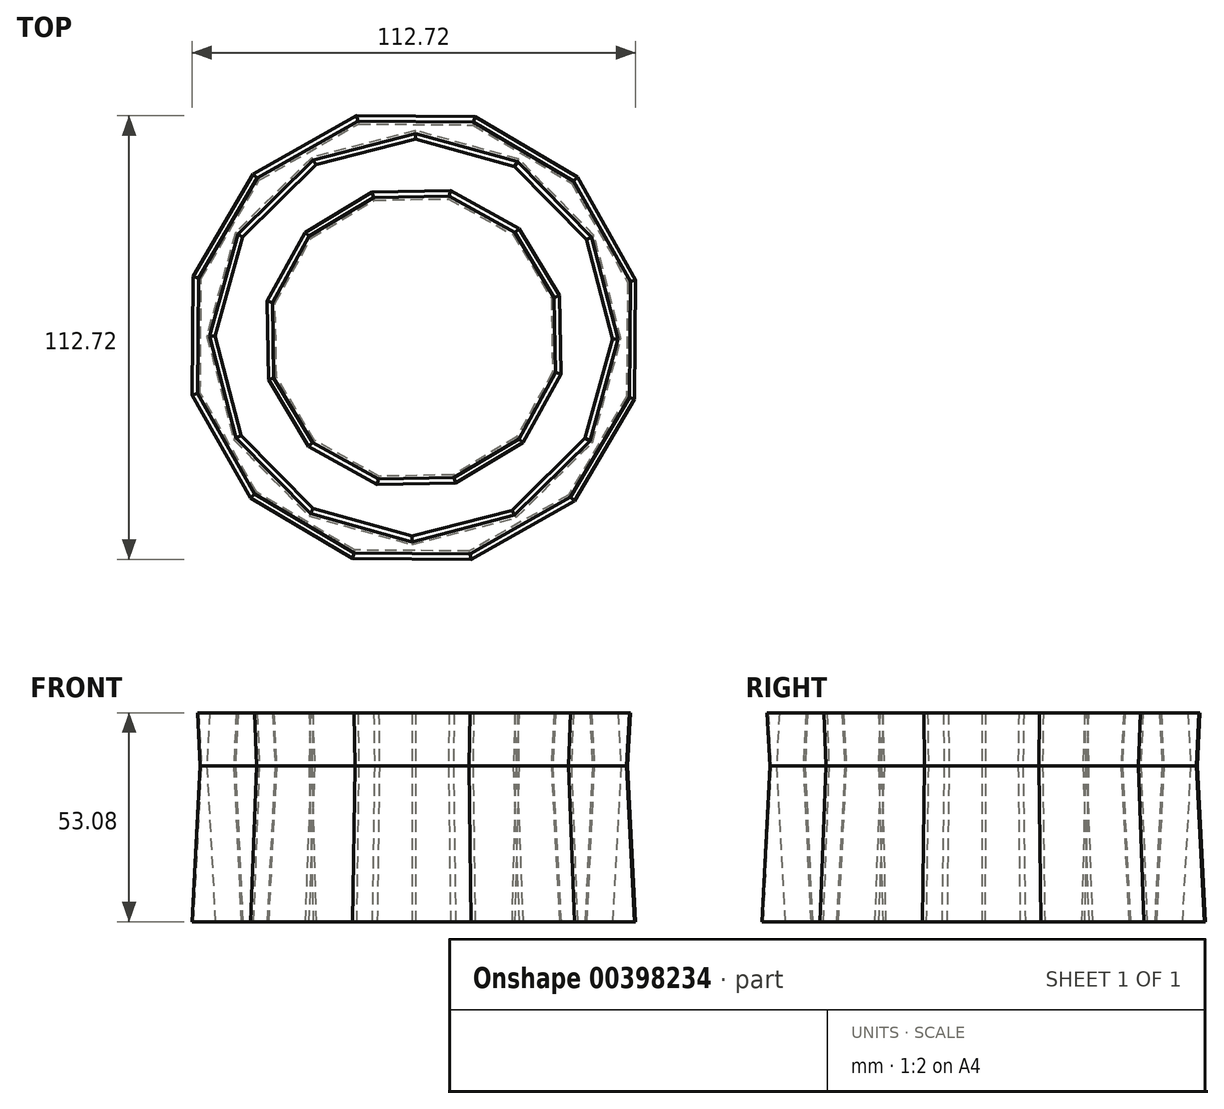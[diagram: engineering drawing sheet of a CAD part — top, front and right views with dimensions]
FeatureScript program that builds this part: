
annotation { "Feature Type Name" : "Feature", "Feature Type Description" : "" }
export const myFeature = defineFeature(function(context is Context, id is Id, definition is map)
    precondition{}
    {
        {
            var Q0;
            Q0=qCreatedBy(makeId("Top.planeOp"),FACE);
            var sketch = newSketch(context, id + "F0", { "sketchPlane" : qUnion([Q0])});
            skCircle(sketch, "E0.cCircle", {"center": v(0, 0) * mm, "radius": 54.15 * mm, "construction": true});
            skLineSegment(sketch, "E0.0", {"start": v(39.99, 39.3) * mm, "end": v(54.27, 14.03) * mm});
            skLineSegment(sketch, "E0.1", {"start": v(54.27, 14.03) * mm, "end": v(54.02, -14.98) * mm});
            skLineSegment(sketch, "E0.2", {"start": v(54.02, -14.98) * mm, "end": v(39.3, -39.99) * mm});
            skLineSegment(sketch, "E0.3", {"start": v(39.3, -39.99) * mm, "end": v(14.03, -54.27) * mm});
            skLineSegment(sketch, "E0.4", {"start": v(14.03, -54.27) * mm, "end": v(-14.98, -54.02) * mm});
            skLineSegment(sketch, "E0.5", {"start": v(-14.98, -54.02) * mm, "end": v(-39.99, -39.3) * mm});
            skLineSegment(sketch, "E0.6", {"start": v(-39.99, -39.3) * mm, "end": v(-54.27, -14.03) * mm});
            skLineSegment(sketch, "E0.7", {"start": v(-54.27, -14.03) * mm, "end": v(-54.02, 14.98) * mm});
            skLineSegment(sketch, "E0.8", {"start": v(-54.02, 14.98) * mm, "end": v(-39.3, 39.99) * mm});
            skLineSegment(sketch, "E0.9", {"start": v(-39.3, 39.99) * mm, "end": v(-14.03, 54.27) * mm});
            skLineSegment(sketch, "E0.10", {"start": v(-14.03, 54.27) * mm, "end": v(14.98, 54.02) * mm});
            skLineSegment(sketch, "E0.11", {"start": v(14.98, 54.02) * mm, "end": v(39.99, 39.3) * mm});
            skPoint(sketch, "E0.0.midPoint", {"position": v(47.13, 26.66) * mm});
            skCircle(sketch, "E1.cCircle", {"center": v(0, 0) * mm, "radius": 50.82 * mm, "construction": true});
            skLineSegment(sketch, "E1.0", {"start": v(45.77, 25.93) * mm, "end": v(52.6, -0.43) * mm});
            skLineSegment(sketch, "E1.1", {"start": v(52.6, -0.43) * mm, "end": v(45.35, -26.68) * mm});
            skLineSegment(sketch, "E1.2", {"start": v(45.35, -26.68) * mm, "end": v(25.93, -45.77) * mm});
            skLineSegment(sketch, "E1.3", {"start": v(25.93, -45.77) * mm, "end": v(-0.43, -52.6) * mm});
            skLineSegment(sketch, "E1.4", {"start": v(-0.43, -52.6) * mm, "end": v(-26.68, -45.35) * mm});
            skLineSegment(sketch, "E1.5", {"start": v(-26.68, -45.35) * mm, "end": v(-45.77, -25.93) * mm});
            skLineSegment(sketch, "E1.6", {"start": v(-45.77, -25.93) * mm, "end": v(-52.6, 0.43) * mm});
            skLineSegment(sketch, "E1.7", {"start": v(-52.6, 0.43) * mm, "end": v(-45.35, 26.68) * mm});
            skLineSegment(sketch, "E1.8", {"start": v(-45.35, 26.68) * mm, "end": v(-25.93, 45.77) * mm});
            skLineSegment(sketch, "E1.9", {"start": v(-25.93, 45.77) * mm, "end": v(0.43, 52.6) * mm});
            skLineSegment(sketch, "E1.10", {"start": v(0.43, 52.6) * mm, "end": v(26.68, 45.35) * mm});
            skLineSegment(sketch, "E1.11", {"start": v(26.68, 45.35) * mm, "end": v(45.77, 25.93) * mm});
            skPoint(sketch, "E1.0.midPoint", {"position": v(49.2, 12.75) * mm});
            skCircle(sketch, "E2.cCircle", {"center": v(0, 0) * mm, "radius": 44.72 * mm, "construction": true});
            skLineSegment(sketch, "E2.0", {"start": v(44.82, 11.6) * mm, "end": v(44.61, -12.37) * mm});
            skLineSegment(sketch, "E2.1", {"start": v(44.61, -12.37) * mm, "end": v(32.45, -33.02) * mm});
            skLineSegment(sketch, "E2.2", {"start": v(32.45, -33.02) * mm, "end": v(11.6, -44.82) * mm});
            skLineSegment(sketch, "E2.3", {"start": v(11.6, -44.82) * mm, "end": v(-12.37, -44.61) * mm});
            skLineSegment(sketch, "E2.4", {"start": v(-12.37, -44.61) * mm, "end": v(-33.02, -32.45) * mm});
            skLineSegment(sketch, "E2.5", {"start": v(-33.02, -32.45) * mm, "end": v(-44.82, -11.6) * mm});
            skLineSegment(sketch, "E2.6", {"start": v(-44.82, -11.6) * mm, "end": v(-44.61, 12.37) * mm});
            skLineSegment(sketch, "E2.7", {"start": v(-44.61, 12.37) * mm, "end": v(-32.45, 33.02) * mm});
            skLineSegment(sketch, "E2.8", {"start": v(-32.45, 33.02) * mm, "end": v(-11.6, 44.82) * mm});
            skLineSegment(sketch, "E2.9", {"start": v(-11.6, 44.82) * mm, "end": v(12.37, 44.61) * mm});
            skLineSegment(sketch, "E2.10", {"start": v(12.37, 44.61) * mm, "end": v(33.02, 32.45) * mm});
            skLineSegment(sketch, "E2.11", {"start": v(33.02, 32.45) * mm, "end": v(44.82, 11.6) * mm});
            skPoint(sketch, "E2.0.midPoint", {"position": v(44.71, -0.4) * mm});
            skCircle(sketch, "E3.cCircle", {"center": v(0, 0) * mm, "radius": 40.47 * mm, "construction": true});
            skLineSegment(sketch, "E3.0", {"start": v(36.41, 20.72) * mm, "end": v(41.9, -0.26) * mm});
            skLineSegment(sketch, "E3.1", {"start": v(41.9, -0.26) * mm, "end": v(36.15, -21.17) * mm});
            skLineSegment(sketch, "E3.2", {"start": v(36.15, -21.17) * mm, "end": v(20.72, -36.41) * mm});
            skLineSegment(sketch, "E3.3", {"start": v(20.72, -36.41) * mm, "end": v(-0.26, -41.9) * mm});
            skLineSegment(sketch, "E3.4", {"start": v(-0.26, -41.9) * mm, "end": v(-21.17, -36.15) * mm});
            skLineSegment(sketch, "E3.5", {"start": v(-21.17, -36.15) * mm, "end": v(-36.41, -20.72) * mm});
            skLineSegment(sketch, "E3.6", {"start": v(-36.41, -20.72) * mm, "end": v(-41.9, 0.26) * mm});
            skLineSegment(sketch, "E3.7", {"start": v(-41.9, 0.26) * mm, "end": v(-36.15, 21.17) * mm});
            skLineSegment(sketch, "E3.8", {"start": v(-36.15, 21.17) * mm, "end": v(-20.72, 36.41) * mm});
            skLineSegment(sketch, "E3.9", {"start": v(-20.72, 36.41) * mm, "end": v(0.26, 41.9) * mm});
            skLineSegment(sketch, "E3.10", {"start": v(0.26, 41.9) * mm, "end": v(21.17, 36.15) * mm});
            skLineSegment(sketch, "E3.11", {"start": v(21.17, 36.15) * mm, "end": v(36.41, 20.72) * mm});
            skPoint(sketch, "E3.0.midPoint", {"position": v(39.15, 10.23) * mm});
            skCircle(sketch, "E4.cCircle", {"center": v(0, 0) * mm, "radius": 35.08 * mm, "construction": true});
            skLineSegment(sketch, "E4.0", {"start": v(-35.24, 8.77) * mm, "end": v(-26.13, 25.22) * mm});
            skLineSegment(sketch, "E4.1", {"start": v(-26.13, 25.22) * mm, "end": v(-10.02, 34.9) * mm});
            skLineSegment(sketch, "E4.2", {"start": v(-10.02, 34.9) * mm, "end": v(8.77, 35.24) * mm});
            skLineSegment(sketch, "E4.3", {"start": v(8.77, 35.24) * mm, "end": v(25.22, 26.13) * mm});
            skLineSegment(sketch, "E4.4", {"start": v(25.22, 26.13) * mm, "end": v(34.9, 10.02) * mm});
            skLineSegment(sketch, "E4.5", {"start": v(34.9, 10.02) * mm, "end": v(35.24, -8.77) * mm});
            skLineSegment(sketch, "E4.6", {"start": v(35.24, -8.77) * mm, "end": v(26.13, -25.22) * mm});
            skLineSegment(sketch, "E4.7", {"start": v(26.13, -25.22) * mm, "end": v(10.02, -34.9) * mm});
            skLineSegment(sketch, "E4.8", {"start": v(10.02, -34.9) * mm, "end": v(-8.77, -35.24) * mm});
            skLineSegment(sketch, "E4.9", {"start": v(-8.77, -35.24) * mm, "end": v(-25.22, -26.13) * mm});
            skLineSegment(sketch, "E4.10", {"start": v(-25.22, -26.13) * mm, "end": v(-34.9, -10.02) * mm});
            skLineSegment(sketch, "E4.11", {"start": v(-34.9, -10.02) * mm, "end": v(-35.24, 8.77) * mm});
            skPoint(sketch, "E4.0.midPoint", {"position": v(-30.69, 17) * mm});
            skCircle(sketch, "E5.cCircle", {"center": v(0, 0) * mm, "radius": 29.08 * mm, "construction": true});
            skLineSegment(sketch, "E5.0", {"start": v(-16.79, 29.08) * mm, "end": v(16.79, 29.08) * mm});
            skLineSegment(sketch, "E5.1", {"start": v(16.79, 29.08) * mm, "end": v(33.58, 0) * mm});
            skLineSegment(sketch, "E5.2", {"start": v(33.58, 0) * mm, "end": v(16.79, -29.08) * mm});
            skLineSegment(sketch, "E5.3", {"start": v(16.79, -29.08) * mm, "end": v(-16.79, -29.08) * mm});
            skLineSegment(sketch, "E5.4", {"start": v(-16.79, -29.08) * mm, "end": v(-33.58, 0) * mm});
            skLineSegment(sketch, "E5.5", {"start": v(-33.58, 0) * mm, "end": v(-16.79, 29.08) * mm});
            skPoint(sketch, "E5.0.midPoint", {"position": v(0, 29.08) * mm});
            skCircle(sketch, "E6.cCircle", {"center": v(0, 0) * mm, "radius": 23.57 * mm, "construction": true});
            skLineSegment(sketch, "E6.0", {"start": v(-23.6, 13.55) * mm, "end": v(-0.07, 27.21) * mm});
            skLineSegment(sketch, "E6.1", {"start": v(-0.07, 27.21) * mm, "end": v(23.53, 13.67) * mm});
            skLineSegment(sketch, "E6.2", {"start": v(23.53, 13.67) * mm, "end": v(23.6, -13.55) * mm});
            skLineSegment(sketch, "E6.3", {"start": v(23.6, -13.55) * mm, "end": v(0.07, -27.21) * mm});
            skLineSegment(sketch, "E6.4", {"start": v(0.07, -27.21) * mm, "end": v(-23.53, -13.67) * mm});
            skLineSegment(sketch, "E6.5", {"start": v(-23.53, -13.67) * mm, "end": v(-23.6, 13.55) * mm});
            skPoint(sketch, "E6.0.midPoint", {"position": v(-11.84, 20.38) * mm});
            skCircle(sketch, "E7.cCircle", {"center": v(0, 0) * mm, "radius": 18.85 * mm, "construction": true});
            skLineSegment(sketch, "E7.0", {"start": v(11.61, 18.41) * mm, "end": v(21.75, -0.85) * mm});
            skLineSegment(sketch, "E7.1", {"start": v(21.75, -0.85) * mm, "end": v(10.14, -19.26) * mm});
            skLineSegment(sketch, "E7.2", {"start": v(10.14, -19.26) * mm, "end": v(-11.61, -18.41) * mm});
            skLineSegment(sketch, "E7.3", {"start": v(-11.61, -18.41) * mm, "end": v(-21.75, 0.85) * mm});
            skLineSegment(sketch, "E7.4", {"start": v(-21.75, 0.85) * mm, "end": v(-10.14, 19.26) * mm});
            skLineSegment(sketch, "E7.5", {"start": v(-10.14, 19.26) * mm, "end": v(11.61, 18.41) * mm});
            skPoint(sketch, "E7.0.midPoint", {"position": v(16.68, 8.78) * mm});
            skCircle(sketch, "E8.cCircle", {"center": v(0, 0) * mm, "radius": 14.7 * mm, "construction": true});
            skLineSegment(sketch, "E8.0", {"start": v(-8.28, 12.18) * mm, "end": v(-6.7, 13.12) * mm, "construction": true});
            skLineSegment(sketch, "E8.1", {"start": v(-6.7, 13.12) * mm, "end": v(-5, 13.85) * mm, "construction": true});
            skLineSegment(sketch, "E8.2", {"start": v(-5, 13.85) * mm, "end": v(-3.22, 14.37) * mm, "construction": true});
            skLineSegment(sketch, "E8.3", {"start": v(-3.22, 14.37) * mm, "end": v(-1.4, 14.66) * mm, "construction": true});
            skLineSegment(sketch, "E8.4", {"start": v(-1.4, 14.66) * mm, "end": v(0.46, 14.72) * mm, "construction": true});
            skLineSegment(sketch, "E8.5", {"start": v(0.46, 14.72) * mm, "end": v(2.3, 14.55) * mm, "construction": true});
            skLineSegment(sketch, "E8.6", {"start": v(2.3, 14.55) * mm, "end": v(4.1, 14.14) * mm, "construction": true});
            skLineSegment(sketch, "E8.7", {"start": v(4.1, 14.14) * mm, "end": v(5.84, 13.52) * mm, "construction": true});
            skLineSegment(sketch, "E8.8", {"start": v(5.84, 13.52) * mm, "end": v(7.49, 12.68) * mm, "construction": true});
            skLineSegment(sketch, "E8.9", {"start": v(7.49, 12.68) * mm, "end": v(9.02, 11.64) * mm, "construction": true});
            skLineSegment(sketch, "E8.10", {"start": v(9.02, 11.64) * mm, "end": v(10.4, 10.42) * mm, "construction": true});
            skLineSegment(sketch, "E8.11", {"start": v(10.4, 10.42) * mm, "end": v(11.63, 9.03) * mm, "construction": true});
            skLineSegment(sketch, "E8.12", {"start": v(11.63, 9.03) * mm, "end": v(12.67, 7.5) * mm, "construction": true});
            skLineSegment(sketch, "E8.13", {"start": v(12.67, 7.5) * mm, "end": v(13.51, 5.86) * mm, "construction": true});
            skLineSegment(sketch, "E8.14", {"start": v(13.51, 5.86) * mm, "end": v(14.14, 4.12) * mm, "construction": true});
            skLineSegment(sketch, "E8.15", {"start": v(14.14, 4.12) * mm, "end": v(14.54, 2.31) * mm, "construction": true});
            skLineSegment(sketch, "E8.16", {"start": v(14.54, 2.31) * mm, "end": v(14.72, 0.47) * mm, "construction": true});
            skLineSegment(sketch, "E8.17", {"start": v(14.72, 0.47) * mm, "end": v(14.66, -1.38) * mm, "construction": true});
            skLineSegment(sketch, "E8.18", {"start": v(14.66, -1.38) * mm, "end": v(14.37, -3.2) * mm, "construction": true});
            skLineSegment(sketch, "E8.19", {"start": v(14.37, -3.2) * mm, "end": v(13.86, -4.98) * mm, "construction": true});
            skLineSegment(sketch, "E8.20", {"start": v(13.86, -4.98) * mm, "end": v(13.12, -6.68) * mm, "construction": true});
            skLineSegment(sketch, "E8.21", {"start": v(13.12, -6.68) * mm, "end": v(12.18, -8.27) * mm, "construction": true});
            skLineSegment(sketch, "E8.22", {"start": v(12.18, -8.27) * mm, "end": v(11.05, -9.73) * mm, "construction": true});
            skLineSegment(sketch, "E8.23", {"start": v(11.05, -9.73) * mm, "end": v(9.74, -11.04) * mm, "construction": true});
            skLineSegment(sketch, "E8.24", {"start": v(9.74, -11.04) * mm, "end": v(8.28, -12.18) * mm, "construction": true});
            skLineSegment(sketch, "E8.25", {"start": v(8.28, -12.18) * mm, "end": v(6.7, -13.12) * mm, "construction": true});
            skLineSegment(sketch, "E8.26", {"start": v(6.7, -13.12) * mm, "end": v(5, -13.85) * mm, "construction": true});
            skLineSegment(sketch, "E8.27", {"start": v(5, -13.85) * mm, "end": v(3.22, -14.37) * mm, "construction": true});
            skLineSegment(sketch, "E8.28", {"start": v(3.22, -14.37) * mm, "end": v(1.4, -14.66) * mm, "construction": true});
            skLineSegment(sketch, "E8.29", {"start": v(1.4, -14.66) * mm, "end": v(-0.46, -14.72) * mm, "construction": true});
            skLineSegment(sketch, "E8.30", {"start": v(-0.46, -14.72) * mm, "end": v(-2.3, -14.55) * mm, "construction": true});
            skLineSegment(sketch, "E8.31", {"start": v(-2.3, -14.55) * mm, "end": v(-4.1, -14.14) * mm, "construction": true});
            skLineSegment(sketch, "E8.32", {"start": v(-4.1, -14.14) * mm, "end": v(-5.84, -13.52) * mm, "construction": true});
            skLineSegment(sketch, "E8.33", {"start": v(-5.84, -13.52) * mm, "end": v(-7.49, -12.68) * mm, "construction": true});
            skLineSegment(sketch, "E8.34", {"start": v(-7.49, -12.68) * mm, "end": v(-9.02, -11.64) * mm, "construction": true});
            skLineSegment(sketch, "E8.35", {"start": v(-9.02, -11.64) * mm, "end": v(-10.4, -10.42) * mm, "construction": true});
            skLineSegment(sketch, "E8.36", {"start": v(-10.4, -10.42) * mm, "end": v(-11.63, -9.03) * mm, "construction": true});
            skLineSegment(sketch, "E8.37", {"start": v(-11.63, -9.03) * mm, "end": v(-12.67, -7.5) * mm, "construction": true});
            skLineSegment(sketch, "E8.38", {"start": v(-12.67, -7.5) * mm, "end": v(-13.51, -5.86) * mm, "construction": true});
            skLineSegment(sketch, "E8.39", {"start": v(-13.51, -5.86) * mm, "end": v(-14.14, -4.12) * mm, "construction": true});
            skLineSegment(sketch, "E8.40", {"start": v(-14.14, -4.12) * mm, "end": v(-14.54, -2.31) * mm, "construction": true});
            skLineSegment(sketch, "E8.41", {"start": v(-14.54, -2.31) * mm, "end": v(-14.72, -0.47) * mm, "construction": true});
            skLineSegment(sketch, "E8.42", {"start": v(-14.72, -0.47) * mm, "end": v(-14.66, 1.38) * mm, "construction": true});
            skLineSegment(sketch, "E8.43", {"start": v(-14.66, 1.38) * mm, "end": v(-14.37, 3.2) * mm, "construction": true});
            skLineSegment(sketch, "E8.44", {"start": v(-14.37, 3.2) * mm, "end": v(-13.86, 4.98) * mm, "construction": true});
            skLineSegment(sketch, "E8.45", {"start": v(-13.86, 4.98) * mm, "end": v(-13.12, 6.68) * mm, "construction": true});
            skLineSegment(sketch, "E8.46", {"start": v(-13.12, 6.68) * mm, "end": v(-12.18, 8.27) * mm, "construction": true});
            skLineSegment(sketch, "E8.47", {"start": v(-12.18, 8.27) * mm, "end": v(-11.05, 9.73) * mm, "construction": true});
            skLineSegment(sketch, "E8.48", {"start": v(-11.05, 9.73) * mm, "end": v(-9.74, 11.04) * mm, "construction": true});
            skLineSegment(sketch, "E8.49", {"start": v(-9.74, 11.04) * mm, "end": v(-8.28, 12.18) * mm, "construction": true});
            skPoint(sketch, "E8.0.midPoint", {"position": v(-7.49, 12.65) * mm});
            skSolve(sketch);
        }
        {
            var Q0;
            Q0=makeQuery(id+"F0.imprint","IMPRINT",FACE,{"disambiguationData":[TD([[makeQuery(id+"F0.imprint","IMPRINT",EDGE,{"derivedFrom":sQuery(id+"F0.wireOp",EDGE,"E0.0")}),-1.0]])]});
            var Q1;
            Q1=makeQuery(id+"F0.imprint","IMPRINT",FACE,{"disambiguationData":[TD([[makeQuery(id+"F0.imprint","IMPRINT",EDGE,{"derivedFrom":sQuery(id+"F0.wireOp",EDGE,"E6.0")}),-1.0]])]});
            var Q2;
            Q2=makeQuery(id+"F0.imprint","IMPRINT",FACE,{"disambiguationData":[TD([[makeQuery(id+"F0.imprint","IMPRINT",EDGE,{"derivedFrom":sQuery(id+"F0.wireOp",EDGE,"E7.0")}),-1.0]])]});
            var Q3;
            Q3=makeQuery(id+"F0.imprint","IMPRINT",FACE,{"disambiguationData":[TD([[makeQuery(id+"F0.imprint","IMPRINT",EDGE,{"derivedFrom":sQuery(id+"F0.wireOp",EDGE,"E4.0")}),-1.0]])]});
            var Q4;
            Q4=makeQuery(id+"F0.imprint","IMPRINT",FACE,{"disambiguationData":[TD([[makeQuery(id+"F0.imprint","IMPRINT",EDGE,{"derivedFrom":sQuery(id+"F0.wireOp",EDGE,"E5.0")}),-1.0]])]});
            extrude(context, id + "F1", {"entities" : qUnion([Q0, Q1, Q2, Q3, Q4]), "depth" : 13.46 * mm, "hasDraft" : true, "draftAngle" : 3 * degree, "hasSecondDirection" : true, "secondDirectionOppositeDirection" : true, "secondDirectionDepth" : 39.62 * mm, "hasSecondDirectionDraft" : true, "secondDirectionDraftAngle" : 3 * degree});
        }
    });
